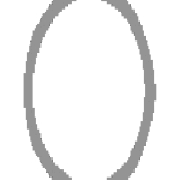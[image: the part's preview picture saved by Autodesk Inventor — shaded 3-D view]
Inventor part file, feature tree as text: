
AUTODESK INVENTOR PART (.ipt)
format: ipt  version: 2021 (Build 250183000, 183)  size: 113,152 bytes
history: native  units: in
note: dims shown in document units (in); Inventor stores cm internally (conversion verified against a paired STEP export)
features: other x4, sketch x3, plane x1
ambient origin geometry x8: Origin, YZ Plane, XZ Plane, XY Plane, X Axis, Y Axis, Z Axis, Center Point
bodies: Solid1 (feature_tree), Body (feature_tree)
feature tree (8):
  other  "Driven Length"
  other  "Frame Generator"
  other  "Start Plane"
  other  "End Plane"
  sketch  "Sketch"  dims[d2=8.3217in d4=-0.0in d5=8.3217in d6=0.12in d7=0.0in d8=90.0deg d9=8.3217in]
  sketch  "Sketch2"  dims[d0=1.0in]
  plane  "Work Plane3"
  sketch  "Sketch3"  dims[d1=0.065in]
